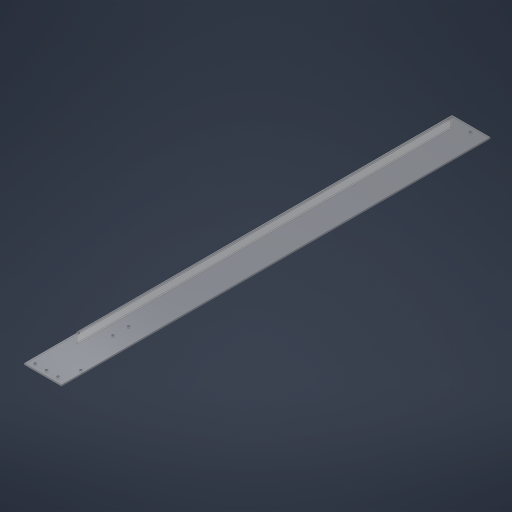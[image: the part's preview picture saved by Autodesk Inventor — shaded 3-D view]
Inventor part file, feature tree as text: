
AUTODESK INVENTOR PART (.ipt)
format: ipt  version: 2023.4 (Build 274418000, 418)  size: 298,496 bytes
history: native  units: in
note: dims shown in document units (in); Inventor stores cm internally (conversion verified against a paired STEP export)
features: sheet_metal_op x4, sketch x3, other x3, hole x2, extrude x1, projected_geometry x1
ambient origin geometry x8: Origin, YZ Plane, XZ Plane, XY Plane, X Axis, Y Axis, Z Axis, Center Point
bodies: Solid1 (feature_tree)
feature tree (14):
  sketch  "Sketch1"  dims[d1=1.5in d2=3.5in]
  sheet_metal_op  "Face1"
  hole  "Hole1"  [1 undecoded]
  hole  "Hole2"  [1 undecoded]
  extrude  "Extrusion1"  Depth=0.125in
  sheet_metal_op  "Flange1"
  other  "Plate1"
  sketch  "Sketch2"  dims[d3=39.375in d4=0.5in]
  sketch  "Sketch3"  dims[d5=5.0in d6=0.5in d7=1.0in d8=1.0in d9=1.375in d10=0.3125in d11=3.1875in d12=3.0in d13=0.25in d14=0.125in d15=0.5in d16=2.5in d17=0.375in d18=37.5in d19=0.17in d20=0.17in d21=0.1in d23=0.201in d26=0.125in d27=0.125in d28=3.5in d29=0.275in d31=0.125in d32=0.201in d33=0.75in d34=0.385in d35=0.25in d36=0.5635in d37=0.125in d38=0.8108in d39=1.375in d40=0.52in d41=0.52in d42=0.52in d43=1.7933in d44=1.345in d45=3.26in d46=1.145in d48=6.0in d49=0.201in d50=0.75in d51=0.375in d52=0.25in d53=0.5635in d54=1.0in d55=0.8108in d56=6.0in d58=0.5in d59=0.0in d60=0.0in d61=2.0in d62=0.125in d63=0.0625in d64=0.25in d65=0.125in d66=1.0in d67=90.0deg d68=0.125in d69=0.5in d70=0.125in d71=0.125in]
  other  "Plate2"
  sheet_metal_op  "Bend1"
  sheet_metal_op  "Corner1"
  projected_geometry  "Project Cut Edges1"
  other  "Definition1"
note: 2 required parameter values undecoded (feature->parameter linkage not recoverable at this tier; creation-order binding heuristic only, values carry confidence <= 0.55)
